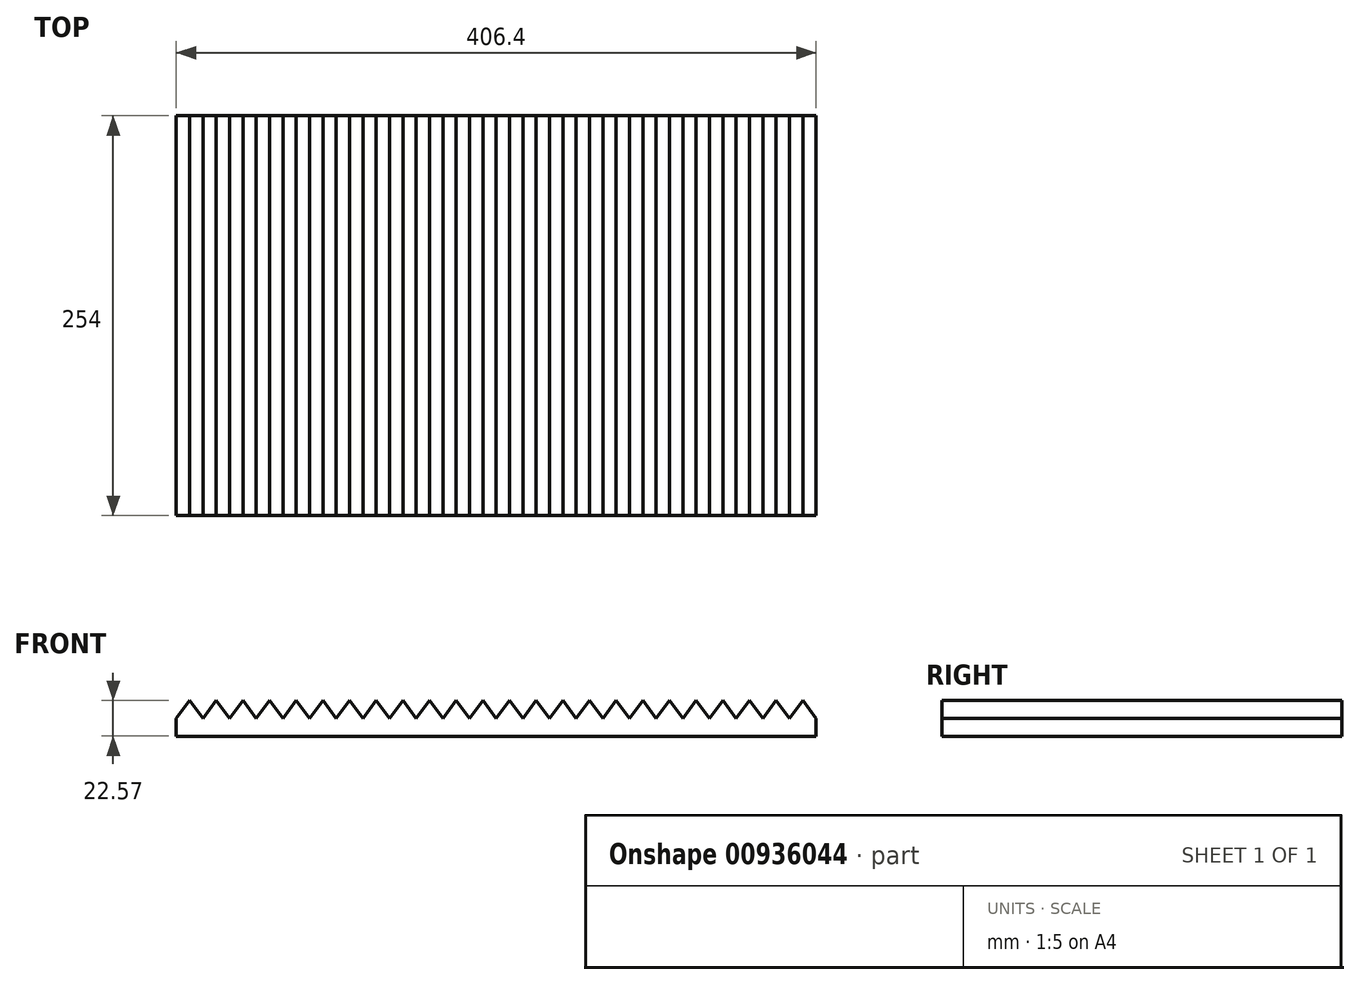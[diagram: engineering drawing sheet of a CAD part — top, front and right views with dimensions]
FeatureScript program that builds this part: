
annotation { "Feature Type Name" : "Feature", "Feature Type Description" : "" }
export const myFeature = defineFeature(function(context is Context, id is Id, definition is map)
    precondition{}
    {
        {
            var Q0;
            Q0=qCreatedBy(makeId("Front.planeOp"),FACE);
            var sketch = newSketch(context, id + "F0", { "sketchPlane" : qUnion([Q0])});
            skLineSegment(sketch, "E0.bottom", {"start": v(-203.2, 5.64) * mm, "end": v(203.2, 5.64) * mm});
            skLineSegment(sketch, "E0.top", {"start": v(-203.2, -5.64) * mm, "end": v(203.2, -5.64) * mm});
            skLineSegment(sketch, "E0.left", {"start": v(-203.2, 5.64) * mm, "end": v(-203.2, -5.64) * mm});
            skLineSegment(sketch, "E0.right", {"start": v(203.2, 5.64) * mm, "end": v(203.2, -5.64) * mm});
            skPoint(sketch, "E0.middle", {"position": v(0, 0) * mm});
            skLineSegment(sketch, "E1", {"start": v(-203.2, 5.64) * mm, "end": v(-186.27, 5.64) * mm});
            skLineSegment(sketch, "E2", {"start": v(-194.73, 5.64) * mm, "end": v(-194.73, 16.93) * mm});
            skLineSegment(sketch, "E3", {"start": v(-203.2, 5.64) * mm, "end": v(-194.73, 16.93) * mm});
            skLineSegment(sketch, "E4", {"start": v(-194.73, 16.93) * mm, "end": v(-186.27, 5.64) * mm});
            skLineSegment(sketch, "E5.direction1", {"start": v(-186.27, 5.64) * mm, "end": v(-151.05, 5.64) * mm, "construction": true});
            skLineSegment(sketch, "E6.1.0.0", {"start": v(-177.8, 16.93) * mm, "end": v(-169.33, 5.64) * mm});
            skLineSegment(sketch, "E6.1.0.1", {"start": v(-186.27, 5.64) * mm, "end": v(-169.33, 5.64) * mm});
            skLineSegment(sketch, "E6.1.0.2", {"start": v(-186.27, 5.64) * mm, "end": v(-177.8, 16.93) * mm});
            skLineSegment(sketch, "E6.2.0.0", {"start": v(-160.87, 16.93) * mm, "end": v(-152.4, 5.64) * mm});
            skLineSegment(sketch, "E6.2.0.1", {"start": v(-169.33, 5.64) * mm, "end": v(-152.4, 5.64) * mm});
            skLineSegment(sketch, "E6.2.0.2", {"start": v(-169.33, 5.64) * mm, "end": v(-160.87, 16.93) * mm});
            skLineSegment(sketch, "E6.3.0.0", {"start": v(-143.93, 16.93) * mm, "end": v(-135.47, 5.64) * mm});
            skLineSegment(sketch, "E6.3.0.1", {"start": v(-152.4, 5.64) * mm, "end": v(-135.47, 5.64) * mm});
            skLineSegment(sketch, "E6.3.0.2", {"start": v(-152.4, 5.64) * mm, "end": v(-143.93, 16.93) * mm});
            skLineSegment(sketch, "E6.4.0.0", {"start": v(-127, 16.93) * mm, "end": v(-118.53, 5.64) * mm});
            skLineSegment(sketch, "E6.4.0.1", {"start": v(-135.47, 5.64) * mm, "end": v(-118.53, 5.64) * mm});
            skLineSegment(sketch, "E6.4.0.2", {"start": v(-135.47, 5.64) * mm, "end": v(-127, 16.93) * mm});
            skLineSegment(sketch, "E6.5.0.0", {"start": v(-110.07, 16.93) * mm, "end": v(-101.6, 5.64) * mm});
            skLineSegment(sketch, "E6.5.0.1", {"start": v(-118.53, 5.64) * mm, "end": v(-101.6, 5.64) * mm});
            skLineSegment(sketch, "E6.5.0.2", {"start": v(-118.53, 5.64) * mm, "end": v(-110.07, 16.93) * mm});
            skLineSegment(sketch, "E6.6.0.0", {"start": v(-93.13, 16.93) * mm, "end": v(-84.67, 5.64) * mm});
            skLineSegment(sketch, "E6.6.0.1", {"start": v(-101.6, 5.64) * mm, "end": v(-84.67, 5.64) * mm});
            skLineSegment(sketch, "E6.6.0.2", {"start": v(-101.6, 5.64) * mm, "end": v(-93.13, 16.93) * mm});
            skLineSegment(sketch, "E6.7.0.0", {"start": v(-76.2, 16.93) * mm, "end": v(-67.73, 5.64) * mm});
            skLineSegment(sketch, "E6.7.0.1", {"start": v(-84.67, 5.64) * mm, "end": v(-67.73, 5.64) * mm});
            skLineSegment(sketch, "E6.7.0.2", {"start": v(-84.67, 5.64) * mm, "end": v(-76.2, 16.93) * mm});
            skLineSegment(sketch, "E6.8.0.0", {"start": v(-59.27, 16.93) * mm, "end": v(-50.8, 5.64) * mm});
            skLineSegment(sketch, "E6.8.0.1", {"start": v(-67.73, 5.64) * mm, "end": v(-50.8, 5.64) * mm});
            skLineSegment(sketch, "E6.8.0.2", {"start": v(-67.73, 5.64) * mm, "end": v(-59.27, 16.93) * mm});
            skLineSegment(sketch, "E6.9.0.0", {"start": v(-42.33, 16.93) * mm, "end": v(-33.87, 5.64) * mm});
            skLineSegment(sketch, "E6.9.0.1", {"start": v(-50.8, 5.64) * mm, "end": v(-33.87, 5.64) * mm});
            skLineSegment(sketch, "E6.9.0.2", {"start": v(-50.8, 5.64) * mm, "end": v(-42.33, 16.93) * mm});
            skLineSegment(sketch, "E6.10.0.0", {"start": v(-25.4, 16.93) * mm, "end": v(-16.93, 5.64) * mm});
            skLineSegment(sketch, "E6.10.0.1", {"start": v(-33.87, 5.64) * mm, "end": v(-16.93, 5.64) * mm});
            skLineSegment(sketch, "E6.10.0.2", {"start": v(-33.87, 5.64) * mm, "end": v(-25.4, 16.93) * mm});
            skLineSegment(sketch, "E6.11.0.0", {"start": v(-8.47, 16.93) * mm, "end": v(0, 5.64) * mm});
            skLineSegment(sketch, "E6.11.0.1", {"start": v(-16.93, 5.64) * mm, "end": v(0, 5.64) * mm});
            skLineSegment(sketch, "E6.11.0.2", {"start": v(-16.93, 5.64) * mm, "end": v(-8.47, 16.93) * mm});
            skLineSegment(sketch, "E6.12.0.0", {"start": v(8.47, 16.93) * mm, "end": v(16.93, 5.64) * mm});
            skLineSegment(sketch, "E6.12.0.1", {"start": v(0, 5.64) * mm, "end": v(16.93, 5.64) * mm});
            skLineSegment(sketch, "E6.12.0.2", {"start": v(0, 5.64) * mm, "end": v(8.47, 16.93) * mm});
            skLineSegment(sketch, "E6.13.0.0", {"start": v(25.4, 16.93) * mm, "end": v(33.87, 5.64) * mm});
            skLineSegment(sketch, "E6.13.0.1", {"start": v(16.93, 5.64) * mm, "end": v(33.87, 5.64) * mm});
            skLineSegment(sketch, "E6.13.0.2", {"start": v(16.93, 5.64) * mm, "end": v(25.4, 16.93) * mm});
            skLineSegment(sketch, "E6.14.0.0", {"start": v(42.33, 16.93) * mm, "end": v(50.8, 5.64) * mm});
            skLineSegment(sketch, "E6.14.0.1", {"start": v(33.87, 5.64) * mm, "end": v(50.8, 5.64) * mm});
            skLineSegment(sketch, "E6.14.0.2", {"start": v(33.87, 5.64) * mm, "end": v(42.33, 16.93) * mm});
            skLineSegment(sketch, "E6.15.0.0", {"start": v(59.27, 16.93) * mm, "end": v(67.73, 5.64) * mm});
            skLineSegment(sketch, "E6.15.0.1", {"start": v(50.8, 5.64) * mm, "end": v(67.73, 5.64) * mm});
            skLineSegment(sketch, "E6.15.0.2", {"start": v(50.8, 5.64) * mm, "end": v(59.27, 16.93) * mm});
            skLineSegment(sketch, "E6.16.0.0", {"start": v(76.2, 16.93) * mm, "end": v(84.67, 5.64) * mm});
            skLineSegment(sketch, "E6.16.0.1", {"start": v(67.73, 5.64) * mm, "end": v(84.67, 5.64) * mm});
            skLineSegment(sketch, "E6.16.0.2", {"start": v(67.73, 5.64) * mm, "end": v(76.2, 16.93) * mm});
            skLineSegment(sketch, "E6.17.0.0", {"start": v(93.13, 16.93) * mm, "end": v(101.6, 5.64) * mm});
            skLineSegment(sketch, "E6.17.0.1", {"start": v(84.67, 5.64) * mm, "end": v(101.6, 5.64) * mm});
            skLineSegment(sketch, "E6.17.0.2", {"start": v(84.67, 5.64) * mm, "end": v(93.13, 16.93) * mm});
            skLineSegment(sketch, "E6.18.0.0", {"start": v(110.07, 16.93) * mm, "end": v(118.53, 5.64) * mm});
            skLineSegment(sketch, "E6.18.0.1", {"start": v(101.6, 5.64) * mm, "end": v(118.53, 5.64) * mm});
            skLineSegment(sketch, "E6.18.0.2", {"start": v(101.6, 5.64) * mm, "end": v(110.07, 16.93) * mm});
            skLineSegment(sketch, "E6.19.0.0", {"start": v(127, 16.93) * mm, "end": v(135.47, 5.64) * mm});
            skLineSegment(sketch, "E6.19.0.1", {"start": v(118.53, 5.64) * mm, "end": v(135.47, 5.64) * mm});
            skLineSegment(sketch, "E6.19.0.2", {"start": v(118.53, 5.64) * mm, "end": v(127, 16.93) * mm});
            skLineSegment(sketch, "E6.20.0.0", {"start": v(143.93, 16.93) * mm, "end": v(152.4, 5.64) * mm});
            skLineSegment(sketch, "E6.20.0.1", {"start": v(135.47, 5.64) * mm, "end": v(152.4, 5.64) * mm});
            skLineSegment(sketch, "E6.20.0.2", {"start": v(135.47, 5.64) * mm, "end": v(143.93, 16.93) * mm});
            skLineSegment(sketch, "E6.21.0.0", {"start": v(160.87, 16.93) * mm, "end": v(169.33, 5.64) * mm});
            skLineSegment(sketch, "E6.21.0.1", {"start": v(152.4, 5.64) * mm, "end": v(169.33, 5.64) * mm});
            skLineSegment(sketch, "E6.21.0.2", {"start": v(152.4, 5.64) * mm, "end": v(160.87, 16.93) * mm});
            skLineSegment(sketch, "E6.22.0.0", {"start": v(177.8, 16.93) * mm, "end": v(186.27, 5.64) * mm});
            skLineSegment(sketch, "E6.22.0.1", {"start": v(169.33, 5.64) * mm, "end": v(186.27, 5.64) * mm});
            skLineSegment(sketch, "E6.22.0.2", {"start": v(169.33, 5.64) * mm, "end": v(177.8, 16.93) * mm});
            skLineSegment(sketch, "E6.23.0.0", {"start": v(194.73, 16.93) * mm, "end": v(203.2, 5.64) * mm});
            skLineSegment(sketch, "E6.23.0.1", {"start": v(186.27, 5.64) * mm, "end": v(203.2, 5.64) * mm});
            skLineSegment(sketch, "E6.23.0.2", {"start": v(186.27, 5.64) * mm, "end": v(194.73, 16.93) * mm});
            skLineSegment(sketch, "E6.direction1", {"start": v(-203.2, 5.64) * mm, "end": v(-186.27, 5.64) * mm, "construction": true});
            skLineSegment(sketch, "E7", {"start": v(-186.27, 5.64) * mm, "end": v(-186.27, 46.63) * mm, "construction": true});
            skSolve(sketch);
        }
        {
            var Q0;
            Q0 = qSketchRegion(id + "F0", true);
            extrude(context, id + "F1", {"entities" : qUnion([Q0]), "depth" : 254 * mm, "offsetDistance" : 25 * mm});
        }
    });
